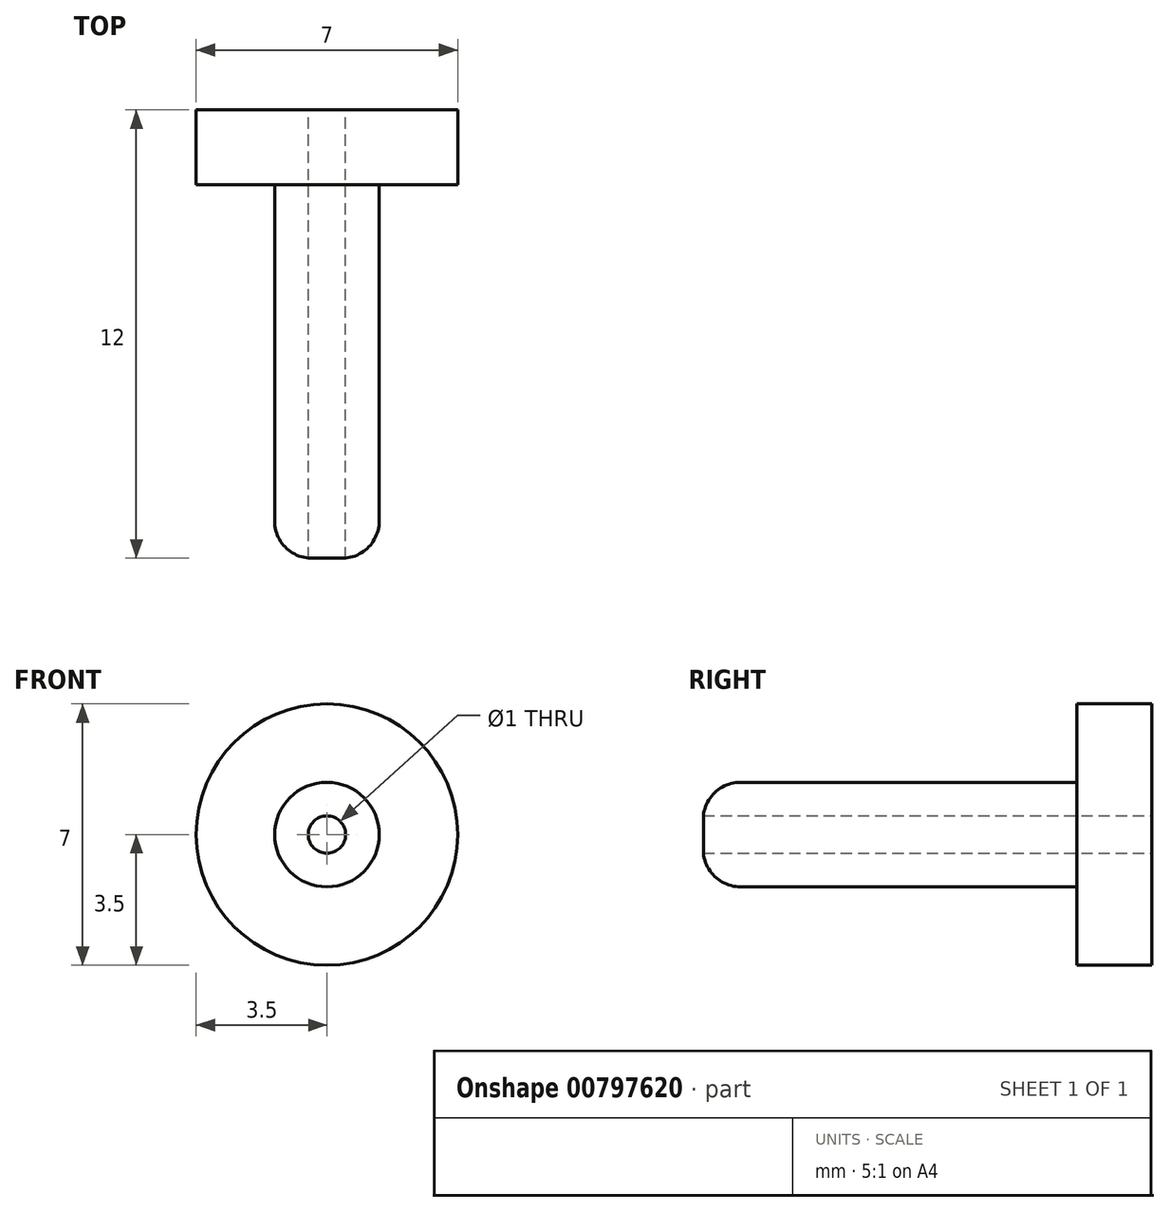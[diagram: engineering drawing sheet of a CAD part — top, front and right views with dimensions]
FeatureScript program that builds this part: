
annotation { "Feature Type Name" : "Feature", "Feature Type Description" : "" }
export const myFeature = defineFeature(function(context is Context, id is Id, definition is map)
    precondition{}
    {
        {
            var Q0;
            Q0=qCreatedBy(makeId("Front.planeOp"),FACE);
            var sketch = newSketch(context, id + "F0", { "sketchPlane" : qUnion([Q0])});
            skCircle(sketch, "E0", {"center": v(0, 0) * mm, "radius": 3.5 * mm});
            skSolve(sketch);
        }
        {
            var Q0;
            Q0=makeQuery(id+"F0.imprint","IMPRINT",FACE,{"disambiguationData":[TD([[makeQuery(id+"F0.imprint","IMPRINT",EDGE,{"derivedFrom":sQuery(id+"F0.wireOp",EDGE,"E0")}),1.0]])]});
            extrude(context, id + "F1", {"entities" : qUnion([Q0]), "depth" : 2 * mm, "offsetDistance" : 25 * mm});
        }
        {
            var Q0;
            Q0=makeQuery(id+"F1.opExtrude","CAP_FACE",FACE,{"disambiguationData":[OSD([sQuery(id+"F0.wireOp",EDGE,"E0")])],"isStart":false});
            var sketch = newSketch(context, id + "F2", { "sketchPlane" : qUnion([Q0])});
            skCircle(sketch, "E1", {"center": v(0, 0) * mm, "radius": 1.4 * mm});
            skSolve(sketch);
        }
        {
            var Q0;
            Q0=makeQuery(id+"F2.imprint","IMPRINT",FACE,{"disambiguationData":[TD([[makeQuery(id+"F2.imprint","IMPRINT",EDGE,{"derivedFrom":sQuery(id+"F2.wireOp",EDGE,"E1")}),1.0]])]});
            extrude(context, id + "F3", {"entities" : qUnion([Q0]), "operationType" : NewBodyOperationType.ADD, "depth" : 10 * mm, "offsetDistance" : 25 * mm});
        }
        {
            var Q0;
            Q0=makeQuery(id+"F1.opExtrude","CAP_FACE",FACE,{"disambiguationData":[OSD([sQuery(id+"F0.wireOp",EDGE,"E0")])],"isStart":true});
            var sketch = newSketch(context, id + "F4", { "sketchPlane" : qUnion([Q0])});
            skCircle(sketch, "E2", {"center": v(0, 0) * mm, "radius": 0.5 * mm});
            skSolve(sketch);
        }
        {
            var Q0;
            Q0=makeQuery(id+"F4.imprint","IMPRINT",FACE,{"disambiguationData":[TD([[makeQuery(id+"F4.imprint","IMPRINT",EDGE,{"derivedFrom":sQuery(id+"F4.wireOp",EDGE,"E2")}),1.0]])]});
            extrude(context, id + "F5", {"entities" : qUnion([Q0]), "operationType" : NewBodyOperationType.REMOVE, "endBound" : BoundingType.THROUGH_ALL, "oppositeDirection" : true, "depth" : 25 * mm, "offsetDistance" : 25 * mm});
        }
        {
            var Q0;
            Q0=makeQuery(id+"F3.opExtrude","CAP_EDGE",EDGE,{"disambiguationData":[OSD([sQuery(id+"F2.wireOp",EDGE,"E1")])],"isStart":false});
            fillet(context, id + "F6", {"entities" : qUnion([Q0]), "radius" : 1 * mm, "tangentPropagation" : true, "allowEdgeOverflow" : false});
        }
    });
